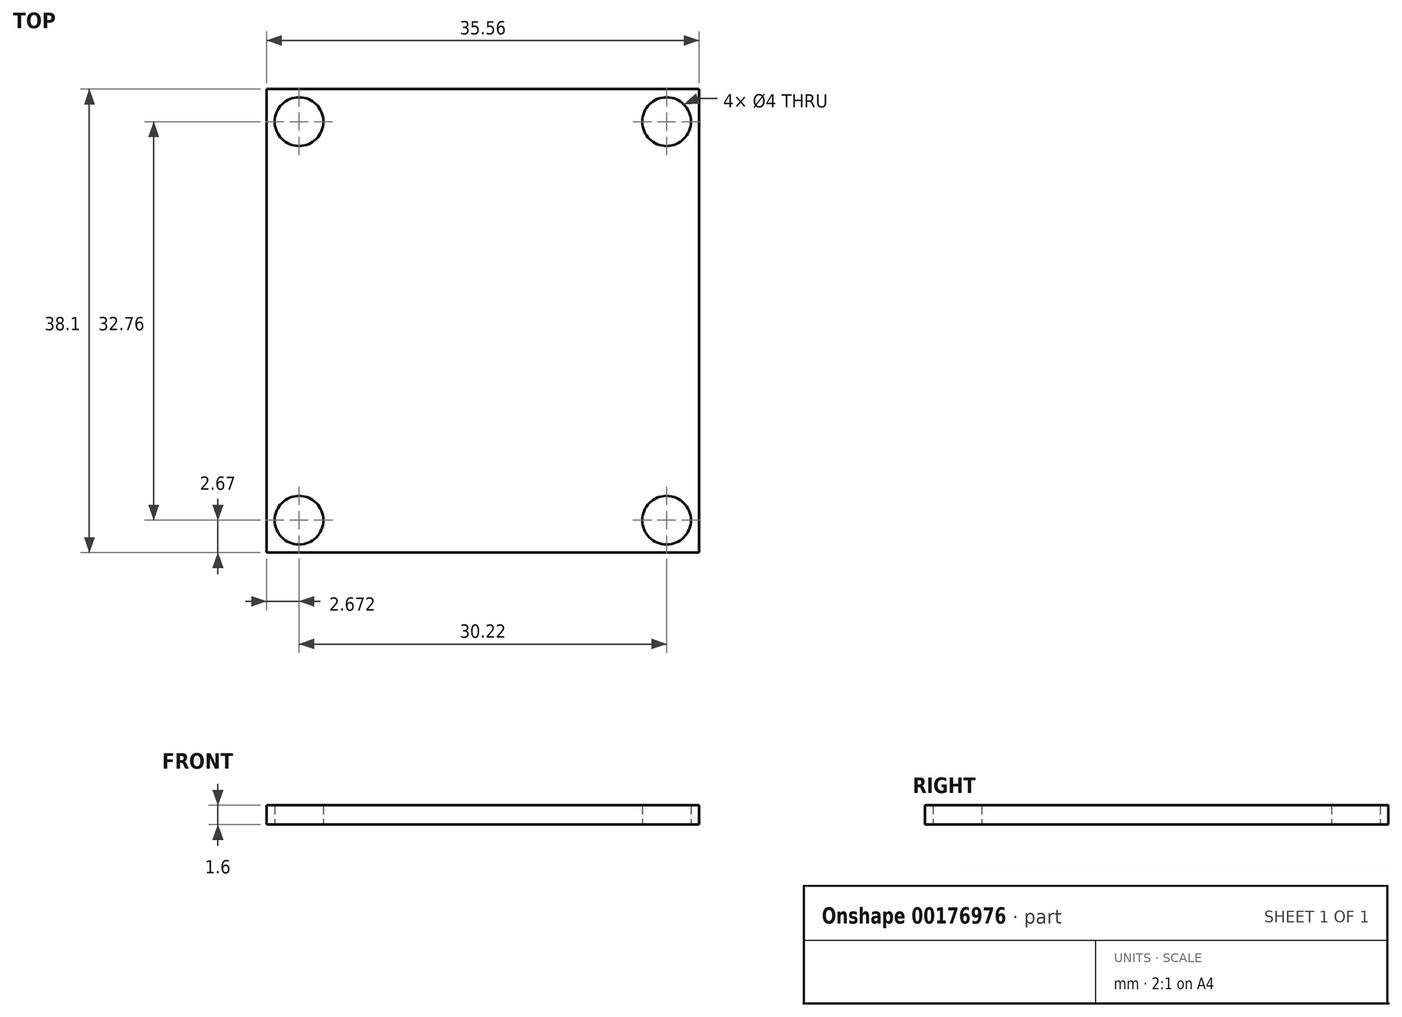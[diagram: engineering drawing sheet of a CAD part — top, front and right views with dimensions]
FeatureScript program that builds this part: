
annotation { "Feature Type Name" : "Feature", "Feature Type Description" : "" }
export const myFeature = defineFeature(function(context is Context, id is Id, definition is map)
    precondition{}
    {
        {
            var Q0;
            Q0=qCreatedBy(makeId("Top.planeOp"),FACE);
            var sketch = newSketch(context, id + "F0", { "sketchPlane" : qUnion([Q0])});
            skLineSegment(sketch, "E0.bottom", {"start": v(-5.4, 11.71) * mm, "end": v(30.16, 11.71) * mm});
            skLineSegment(sketch, "E0.top", {"start": v(-5.4, -26.39) * mm, "end": v(30.16, -26.39) * mm});
            skLineSegment(sketch, "E0.left", {"start": v(-5.4, 11.71) * mm, "end": v(-5.4, -26.39) * mm});
            skLineSegment(sketch, "E0.right", {"start": v(30.16, 11.71) * mm, "end": v(30.16, -26.39) * mm});
            skCircle(sketch, "E1", {"center": v(-2.73, 9.04) * mm, "radius": 2 * mm});
            skLineSegment(sketch, "E2", {"start": v(12.38, 11.71) * mm, "end": v(12.38, -26.39) * mm, "construction": true});
            skCircle(sketch, "E3.MirrorC", {"center": v(27.5, 9.04) * mm, "radius": 2 * mm});
            skLineSegment(sketch, "E4", {"start": v(-5.4, -7.34) * mm, "end": v(30.16, -7.34) * mm, "construction": true});
            skCircle(sketch, "E5.MirrorC", {"center": v(-2.73, -23.72) * mm, "radius": 2 * mm});
            skCircle(sketch, "E6.MirrorC", {"center": v(27.5, -23.72) * mm, "radius": 2 * mm});
            skSolve(sketch);
        }
        {
            var Q0;
            Q0=makeQuery(id+"F0.imprint","IMPRINT",FACE,{"disambiguationData":[TD([[makeQuery(id+"F0.imprint","IMPRINT",EDGE,{"derivedFrom":sQuery(id+"F0.wireOp",EDGE,"E0.bottom")}),-1.0]])]});
            extrude(context, id + "F1", {"entities" : qUnion([Q0]), "depth" : 1.6 * mm, "offsetDistance" : 25 * mm});
        }
    });
